# Revit family: Faucet-Lavatory-KOHLER-Singulier-K-10860M_1
name_source: partatom
category: Plumbing Fixtures
revit_build: Autodesk Revit 2017 (Build: 20160225_1515(x64)
units: mm (PartAtom-declared; Revit-internal decimal feet)

## family parameters
Cut with Voids When Loaded = No
Host = Face
OmniClass Number = 23.31.11.00
OmniClass Title = Faucets
Part Type = Normal
Room Calculation Point = No
Round Connector Dimension = Use Diameter
Shared = No

## types (1)
- CP-Polished Chrome
    ADA Compliant = No
    Assembly Code = D2010
    CW Connection = Yes
    Cold Water Inlet = Cold Water Inlet
    Date Modified = 06/29/2020
    Default Elevation = 36"
    Description = Mixer tap for single handle
    Drain Included = Yes
    Finish = Kohler-Metal-CP-Polished_Chrome
    Flow Rate = 2 GPM
    HW Connection = Yes
    Handle Clearance = 3 3/8"
    Height = 7 1/16"
    Hot Water Inlet = Hot Water Inlet
    Length = 3 15/16"
    Manufacturer = KOHLER Co.
444 Highland Dr.
Kohler, WI 53044
    Master Format 2014 Name = Residential Faucets, Supplies, and Trim
    MasterFormat 2014 = 22.41.39
    Material = Solid Brass Construction
    Model = K-10860M-4-CP
    Pressure = 60.00 psi
    Product Documentation Link = http://resources.kohler.com
    Product Name = Singulier
    Product Page URL = https://la.kohler.com
    Spout Reach = 3 15/16"
    URL = https://la.kohler.com
    Vent Connection = No
    WFU = 0
    Waste Connection = No
    Waste Water Outlet = Waste Water Outlet
    WaterSense Certified = No
    Width = 1 7/8"

## geometry (parser evidence)
native form markers: Sweep x6
no freeform markers — native parametric forms only
